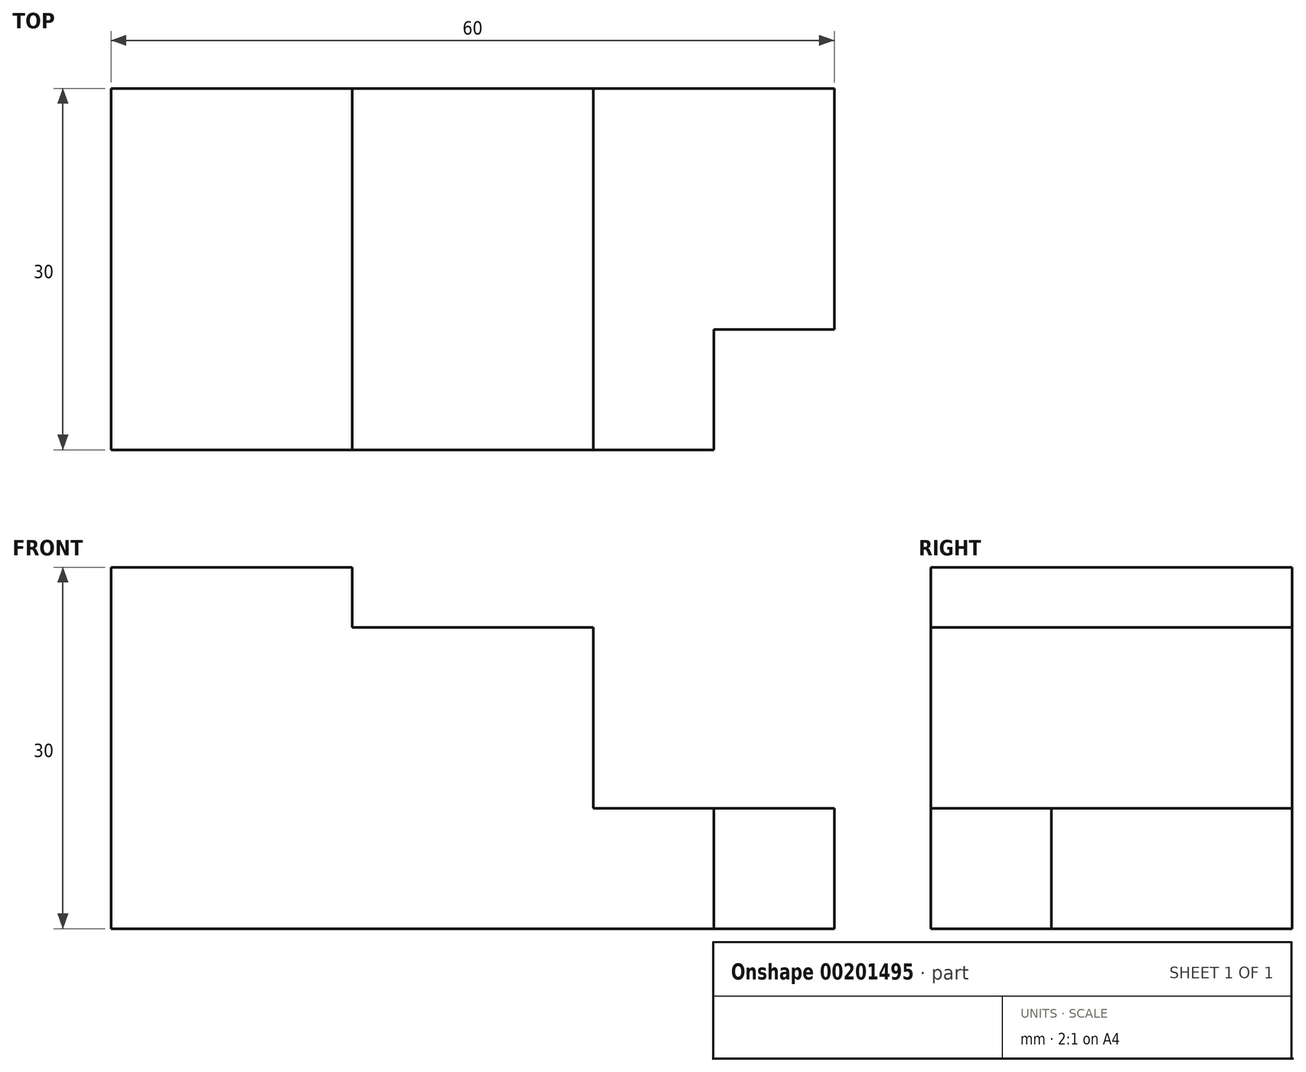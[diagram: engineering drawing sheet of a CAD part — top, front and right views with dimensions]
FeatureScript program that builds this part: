
annotation { "Feature Type Name" : "Feature", "Feature Type Description" : "" }
export const myFeature = defineFeature(function(context is Context, id is Id, definition is map)
    precondition{}
    {
        {
            var Q0;
            Q0=qCreatedBy(makeId("Front.planeOp"),FACE);
            var sketch = newSketch(context, id + "F0", { "sketchPlane" : qUnion([Q0])});
            skLineSegment(sketch, "E0", {"start": v(0, 0) * mm, "end": v(-60, 0) * mm});
            skLineSegment(sketch, "E1", {"start": v(-60, 0) * mm, "end": v(-60, 30) * mm});
            skLineSegment(sketch, "E2", {"start": v(-60, 30) * mm, "end": v(-40, 30) * mm});
            skLineSegment(sketch, "E3", {"start": v(-40, 30) * mm, "end": v(-40, 25) * mm});
            skLineSegment(sketch, "E4", {"start": v(-40, 25) * mm, "end": v(-20, 25) * mm});
            skLineSegment(sketch, "E5", {"start": v(-20, 25) * mm, "end": v(-20, 10) * mm});
            skLineSegment(sketch, "E6", {"start": v(-20, 10) * mm, "end": v(0, 10) * mm});
            skLineSegment(sketch, "E7", {"start": v(0, 10) * mm, "end": v(0, 0) * mm});
            skSolve(sketch);
        }
        {
            var Q0;
            Q0=qSketchRegion(id+"F0",true);
            extrude(context, id + "F1", {"entities" : qUnion([Q0]), "oppositeDirection" : true, "depth" : 30 * mm});
        }
        {
            var Q0;
            Q0=makeQuery(id+"F1.opExtrude","SWEPT_FACE",FACE,{"disambiguationData":[OSD([sQuery(id+"F0.wireOp",EDGE,"E6")])]});
            var sketch = newSketch(context, id + "F2", { "sketchPlane" : qUnion([Q0])});
            skLineSegment(sketch, "E8", {"start": v(-10, 10) * mm, "end": v(0, 10) * mm});
            skLineSegment(sketch, "E9", {"start": v(-10, 10) * mm, "end": v(-10, 0) * mm});
            skSolve(sketch);
        }
        {
            var Q0;
            {var subQ0=sQuery(id+"F2.wireOp",EDGE,"E8");Q0=makeQuery(id+"F2.imprint","IMPRINT",FACE,{"disambiguationData":[TD([[makeQuery(id+"F2.imprint","IMPRINT",EDGE,{"derivedFrom":subQ0}),-1.0]])]});}
            extrude(context, id + "F3", {"entities" : qUnion([Q0]), "operationType" : NewBodyOperationType.REMOVE, "endBound" : BoundingType.THROUGH_ALL, "oppositeDirection" : true, "depth" : 25 * mm});
        }
    });
